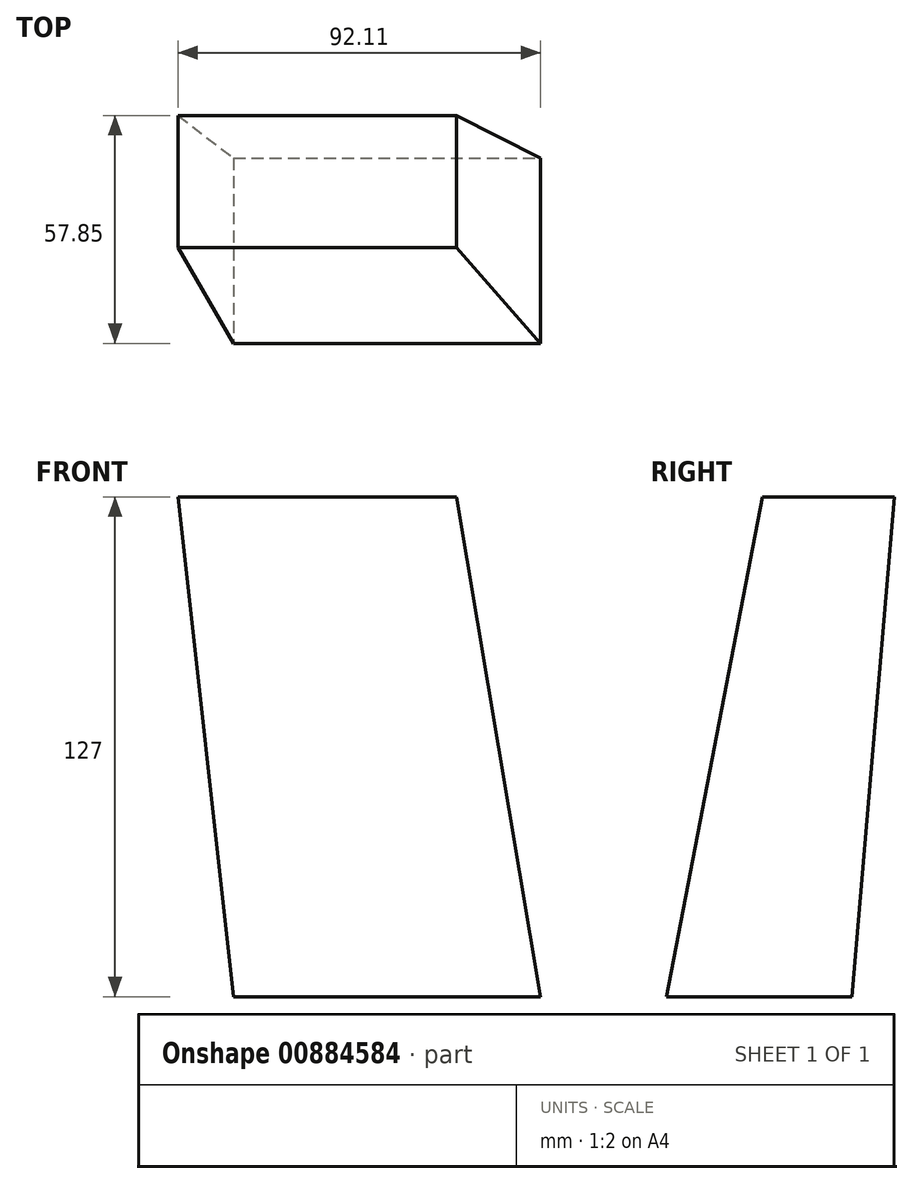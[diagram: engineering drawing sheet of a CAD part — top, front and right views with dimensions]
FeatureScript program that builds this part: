
annotation { "Feature Type Name" : "Feature", "Feature Type Description" : "" }
export const myFeature = defineFeature(function(context is Context, id is Id, definition is map)
    precondition{}
    {
        {
            var Q0;
            Q0=qCreatedBy(makeId("Top.planeOp"),FACE);
            cPlane(context, id + "F0", {"entities" : qUnion([Q0]), "cplaneType" : CPlaneType.OFFSET, "offset" : 127 * mm, "width" : 152.4 * mm, "height" : 152.4 * mm});
        }
        {
            var Q0;
            Q0=qCreatedBy(id+"F0.planeOp",FACE);
            var sketch = newSketch(context, id + "F1", { "sketchPlane" : qUnion([Q0])});
            skLineSegment(sketch, "E0.bottom", {"start": v(-52.36, 0) * mm, "end": v(18.34, 0) * mm});
            skLineSegment(sketch, "E0.top", {"start": v(-52.36, 33.52) * mm, "end": v(18.34, 33.52) * mm});
            skLineSegment(sketch, "E0.left", {"start": v(-52.36, 0) * mm, "end": v(-52.36, 33.52) * mm});
            skLineSegment(sketch, "E0.right", {"start": v(18.34, 0) * mm, "end": v(18.34, 33.52) * mm});
            skSolve(sketch);
        }
        {
            var Q0;
            Q0=qCreatedBy(makeId("Top.planeOp"),FACE);
            var sketch = newSketch(context, id + "F2", { "sketchPlane" : qUnion([Q0])});
            skLineSegment(sketch, "E1.bottom", {"start": v(-38.25, 22.72) * mm, "end": v(39.75, 22.72) * mm});
            skLineSegment(sketch, "E1.top", {"start": v(-38.25, -24.33) * mm, "end": v(39.75, -24.33) * mm});
            skLineSegment(sketch, "E1.left", {"start": v(-38.25, 22.72) * mm, "end": v(-38.25, -24.33) * mm});
            skLineSegment(sketch, "E1.right", {"start": v(39.75, 22.72) * mm, "end": v(39.75, -24.33) * mm});
            skSolve(sketch);
        }
        {
            var Q0;
            Q0=makeQuery(id+"F1.imprint","IMPRINT",FACE,{"disambiguationData":[TD([[makeQuery(id+"F1.imprint","IMPRINT",EDGE,{"derivedFrom":sQuery(id+"F1.wireOp",EDGE,"E0.bottom")}),1.0]])]});
            var Q1;
            Q1=makeQuery(id+"F2.imprint","IMPRINT",FACE,{"disambiguationData":[TD([[makeQuery(id+"F2.imprint","IMPRINT",EDGE,{"derivedFrom":sQuery(id+"F2.wireOp",EDGE,"E1.bottom")}),-1.0]])]});
            loft(context, id + "F3", {"sheetProfilesArray" : [{ "sheetProfileEntities" : qUnion([Q0]) }, { "sheetProfileEntities" : qUnion([Q1]) }]});
        }
    });
